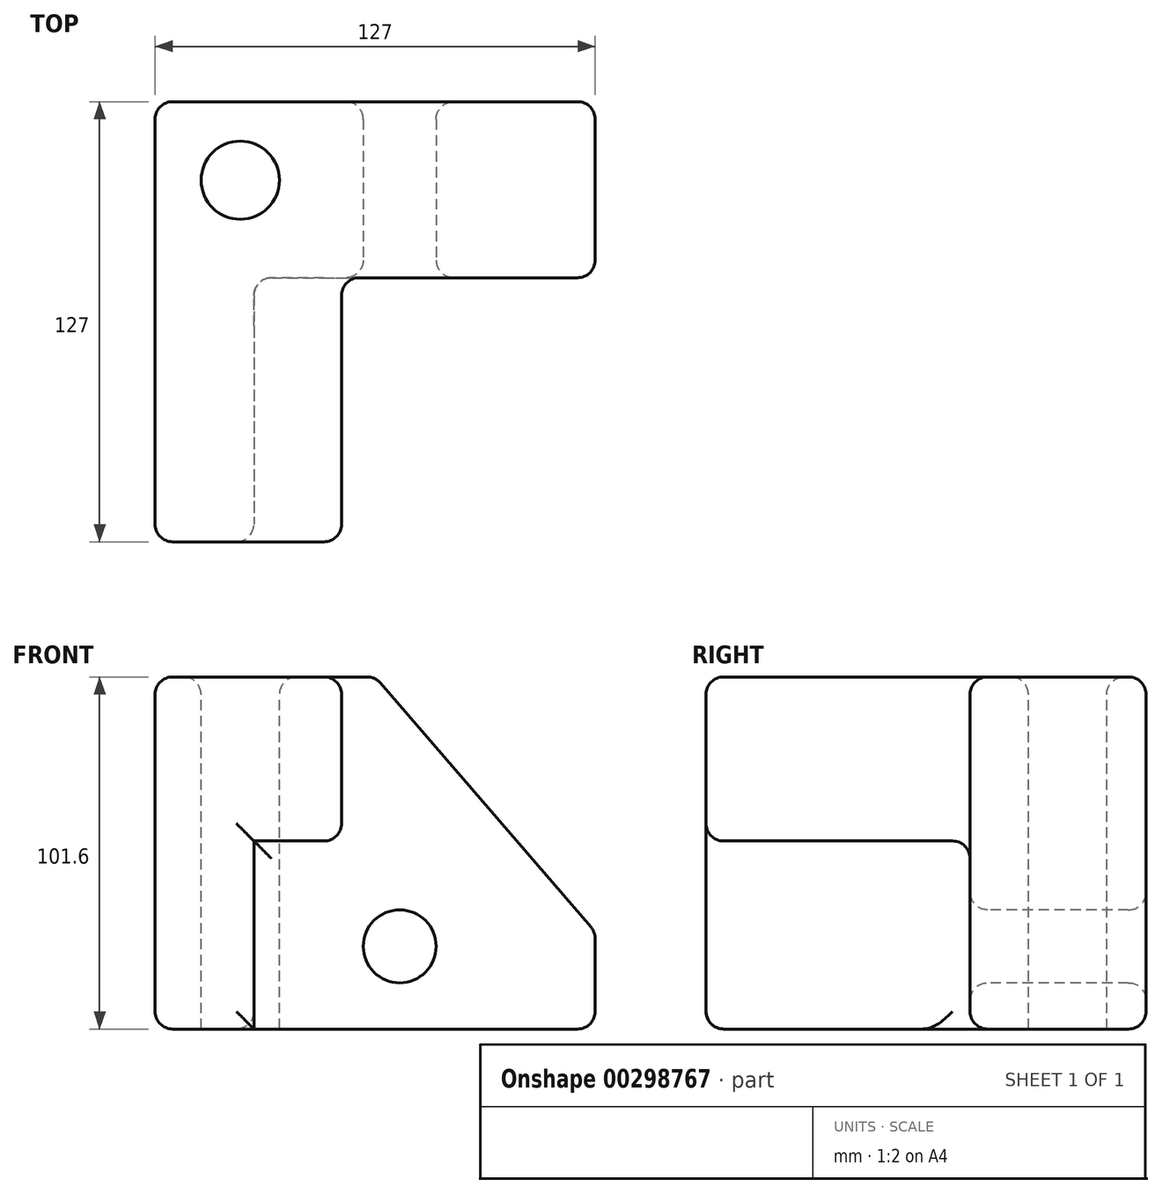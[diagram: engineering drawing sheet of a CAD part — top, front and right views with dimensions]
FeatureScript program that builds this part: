
annotation { "Feature Type Name" : "Feature", "Feature Type Description" : "" }
export const myFeature = defineFeature(function(context is Context, id is Id, definition is map)
    precondition{}
    {
        {
            var Q0;
            Q0=qCreatedBy(makeId("Front.planeOp"),FACE);
            var sketch = newSketch(context, id + "F0", { "sketchPlane" : qUnion([Q0])});
            skLineSegment(sketch, "E0.bottom", {"start": v(-53.82, 47.34) * mm, "end": v(73.18, 47.34) * mm});
            skLineSegment(sketch, "E0.top", {"start": v(-53.82, -54.26) * mm, "end": v(73.18, -54.26) * mm});
            skLineSegment(sketch, "E0.left", {"start": v(-53.82, 47.34) * mm, "end": v(-53.82, -54.26) * mm});
            skLineSegment(sketch, "E0.right", {"start": v(73.18, 47.34) * mm, "end": v(73.18, -54.26) * mm});
            skSolve(sketch);
        }
        {
            var Q0;
            Q0=makeQuery(id+"F0.imprint","IMPRINT",FACE,{"disambiguationData":[TD([[makeQuery(id+"F0.imprint","IMPRINT",EDGE,{"derivedFrom":sQuery(id+"F0.wireOp",EDGE,"E0.bottom")}),-1.0]])]});
            extrude(context, id + "F1", {"entities" : qUnion([Q0]), "depth" : 127 * mm});
        }
        {
            var Q0;
            Q0=makeQuery(id+"F1.opExtrude","CAP_FACE",FACE,{"disambiguationData":[OSD([sQuery(id+"F0.wireOp",EDGE,"E0.bottom"),sQuery(id+"F0.wireOp",EDGE,"E0.top"),sQuery(id+"F0.wireOp",EDGE,"E0.left"),sQuery(id+"F0.wireOp",EDGE,"E0.right")])],"isStart":false});
            var sketch = newSketch(context, id + "F2", { "sketchPlane" : qUnion([Q0])});
            skLineSegment(sketch, "E1", {"start": v(0, 47.34) * mm, "end": v(0, 0) * mm});
            skLineSegment(sketch, "E2", {"start": v(0, 47.34) * mm, "end": v(-53.82, 47.34) * mm});
            skLineSegment(sketch, "E3", {"start": v(-53.82, -54.26) * mm, "end": v(-53.82, 47.34) * mm});
            skLineSegment(sketch, "E4", {"start": v(0, 0) * mm, "end": v(-25.3, 0) * mm});
            skLineSegment(sketch, "E5", {"start": v(-25.3, 0) * mm, "end": v(-25.3, -54.26) * mm});
            skLineSegment(sketch, "E6", {"start": v(-25.3, -54.26) * mm, "end": v(-53.82, -54.26) * mm});
            skSolve(sketch);
        }
        {
            var Q0;
            {var subQ2=sQuery(id+"F2.wireOp",EDGE,"E1");Q0=makeQuery(id+"F2.imprint","IMPRINT",FACE,{"disambiguationData":[TD([[makeQuery(id+"F2.imprint","IMPRINT",EDGE,{"derivedFrom":subQ2}),1.0]])]});}
            extrude(context, id + "F3", {"entities" : qUnion([Q0]), "operationType" : NewBodyOperationType.REMOVE, "oppositeDirection" : true, "depth" : 76.2 * mm});
        }
        {
            var Q0;
            Q0=makeQuery(id+"F3.boolean.opBoolean","COPY",FACE,{"derivedFrom":makeQuery(id+"F3.opExtrude","CAP_FACE",FACE,{"disambiguationData":[OSD([sQuery(id+"F0.wireOp",EDGE,"E0.bottom"),sQuery(id+"F0.wireOp",EDGE,"E0.top"),sQuery(id+"F0.wireOp",EDGE,"E0.right"),sQuery(id+"F2.wireOp",EDGE,"E1"),sQuery(id+"F2.wireOp",EDGE,"E4"),sQuery(id+"F2.wireOp",EDGE,"E5")])],"isStart":false})});
            var sketch = newSketch(context, id + "F4", { "sketchPlane" : qUnion([Q0])});
            skCircle(sketch, "E7", {"center": v(16.77, -30.4) * mm, "radius": 10.52 * mm});
            skSolve(sketch);
        }
        {
            var Q0;
            Q0=makeQuery(id+"F4.imprint","IMPRINT",FACE,{"disambiguationData":[TD([[makeQuery(id+"F4.imprint","IMPRINT",EDGE,{"derivedFrom":sQuery(id+"F4.wireOp",EDGE,"E7")}),1.0]])]});
            extrude(context, id + "F5", {"entities" : qUnion([Q0]), "operationType" : NewBodyOperationType.REMOVE, "endBound" : BoundingType.THROUGH_ALL, "oppositeDirection" : true, "depth" : 25.4 * mm});
        }
        {
            var Q0;
            Q0=makeQuery(id+"F1.opExtrude","SWEPT_FACE",FACE,{"disambiguationData":[OSD([sQuery(id+"F0.wireOp",EDGE,"E0.bottom")])]});
            var sketch = newSketch(context, id + "F6", { "sketchPlane" : qUnion([Q0])});
            skCircle(sketch, "E8", {"center": v(-29.26, -22.67) * mm, "radius": 11.3 * mm});
            skSolve(sketch);
        }
        {
            var Q0;
            Q0=makeQuery(id+"F6.imprint","IMPRINT",FACE,{"disambiguationData":[TD([[makeQuery(id+"F6.imprint","IMPRINT",EDGE,{"derivedFrom":sQuery(id+"F6.wireOp",EDGE,"E8")}),1.0]])]});
            extrude(context, id + "F7", {"entities" : qUnion([Q0]), "operationType" : NewBodyOperationType.REMOVE, "endBound" : BoundingType.THROUGH_ALL, "oppositeDirection" : true, "depth" : 25.4 * mm});
        }
        {
            var Q0;
            Q0=makeQuery(id+"F1.opExtrude","SWEPT_EDGE",EDGE,{"disambiguationData":[OSD([sQuery(id+"F0.wireOp",EDGE,"E0.bottom"),sQuery(id+"F0.wireOp",EDGE,"E0.right")])]});
            chamfer(context, id + "F8", {"entities" : qUnion([Q0]), "chamferType" : ChamferType.TWO_OFFSETS, "width1" : 63.5 * mm, "oppositeDirection" : false, "width2" : 73.66 * mm, "tangentPropagation" : true});
        }
        {
            var Q0;
            Q0=makeQuery(id+"F1.opExtrude","CAP_EDGE",EDGE,{"disambiguationData":[OSD([sQuery(id+"F0.wireOp",EDGE,"E0.bottom")])],"isStart":false});
            var Q1;
            Q1=makeQuery(id+"F1.opExtrude","CAP_FACE",FACE,{"disambiguationData":[OSD([sQuery(id+"F0.wireOp",EDGE,"E0.bottom"),sQuery(id+"F0.wireOp",EDGE,"E0.top"),sQuery(id+"F0.wireOp",EDGE,"E0.left"),sQuery(id+"F0.wireOp",EDGE,"E0.right")])],"isStart":false});
            var Q2;
            Q2=makeQuery(id+"F3.boolean.opBoolean","COPY",FACE,{"derivedFrom":makeQuery(id+"F3.opExtrude","SWEPT_FACE",FACE,{"disambiguationData":[OSD([sQuery(id+"F2.wireOp",EDGE,"E1")])]})});
            var Q3;
            Q3=makeQuery(id+"F1.opExtrude","SWEPT_FACE",FACE,{"disambiguationData":[OSD([sQuery(id+"F0.wireOp",EDGE,"E0.bottom")])]});
            var Q4;
            Q4=makeQuery(id+"F8.opChamfer","BLEND_FACE",FACE,{"disambiguationData":[OSD([sQuery(id+"F0.wireOp",EDGE,"E0.bottom"),sQuery(id+"F0.wireOp",EDGE,"E0.right")])]});
            var Q5;
            Q5=makeQuery(id+"F3.boolean.opBoolean","COPY",FACE,{"derivedFrom":makeQuery(id+"F3.opExtrude","CAP_FACE",FACE,{"disambiguationData":[OSD([sQuery(id+"F0.wireOp",EDGE,"E0.bottom"),sQuery(id+"F0.wireOp",EDGE,"E0.top"),sQuery(id+"F0.wireOp",EDGE,"E0.right"),sQuery(id+"F2.wireOp",EDGE,"E1"),sQuery(id+"F2.wireOp",EDGE,"E4"),sQuery(id+"F2.wireOp",EDGE,"E5")])],"isStart":false})});
            var Q6;
            Q6=makeQuery(id+"F1.opExtrude","SWEPT_FACE",FACE,{"disambiguationData":[OSD([sQuery(id+"F0.wireOp",EDGE,"E0.right")])]});
            var Q7;
            Q7=makeQuery(id+"F1.opExtrude","CAP_FACE",FACE,{"disambiguationData":[OSD([sQuery(id+"F0.wireOp",EDGE,"E0.bottom"),sQuery(id+"F0.wireOp",EDGE,"E0.top"),sQuery(id+"F0.wireOp",EDGE,"E0.left"),sQuery(id+"F0.wireOp",EDGE,"E0.right")])],"isStart":true});
            var Q8;
            Q8=makeQuery(id+"F1.opExtrude","SWEPT_FACE",FACE,{"disambiguationData":[OSD([sQuery(id+"F0.wireOp",EDGE,"E0.left")])]});
            fillet(context, id + "F9", {"entities" : qUnion([Q0, Q1, Q2, Q3, Q4, Q5, Q6, Q7, Q8]), "radius" : 5.08 * mm, "tangentPropagation" : true, "allowEdgeOverflow" : false});
        }
    });
